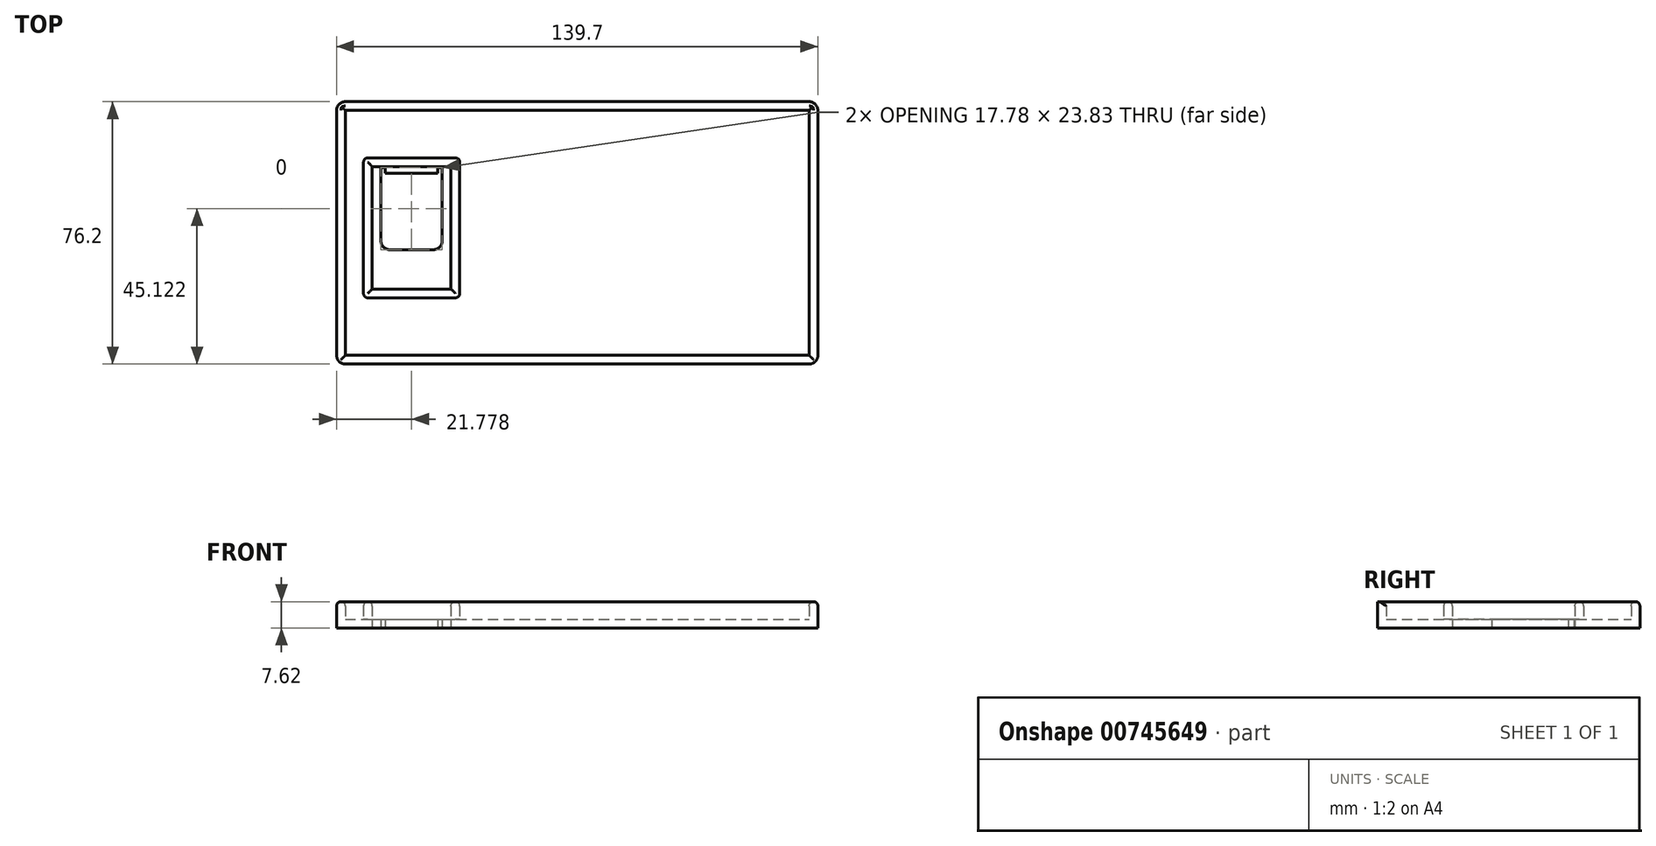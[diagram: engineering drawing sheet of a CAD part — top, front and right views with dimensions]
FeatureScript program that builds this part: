
annotation { "Feature Type Name" : "Feature", "Feature Type Description" : "" }
export const myFeature = defineFeature(function(context is Context, id is Id, definition is map)
    precondition{}
    {
        {
            var Q0;
            Q0=qCreatedBy(makeId("Top.planeOp"),FACE);
            var sketch = newSketch(context, id + "F0", { "sketchPlane" : qUnion([Q0])});
            skLineSegment(sketch, "E0.bottom", {"start": v(-71.99, 34.55) * mm, "end": v(67.71, 34.55) * mm});
            skLineSegment(sketch, "E0.top", {"start": v(-71.99, -41.65) * mm, "end": v(67.71, -41.65) * mm});
            skLineSegment(sketch, "E0.left", {"start": v(-71.99, 34.55) * mm, "end": v(-71.99, -41.65) * mm});
            skLineSegment(sketch, "E0.right", {"start": v(67.71, 34.55) * mm, "end": v(67.71, -41.65) * mm});
            skLineSegment(sketch, "E1.bottom", {"start": v(-69.45, -39.12) * mm, "end": v(65.17, -39.12) * mm});
            skLineSegment(sketch, "E1.top", {"start": v(-69.45, 32.01) * mm, "end": v(65.17, 32.01) * mm});
            skLineSegment(sketch, "E1.left", {"start": v(-69.45, -39.12) * mm, "end": v(-69.45, 32.01) * mm});
            skLineSegment(sketch, "E1.right", {"start": v(65.17, -39.12) * mm, "end": v(65.17, 32.01) * mm});
            skLineSegment(sketch, "E2", {"start": v(-69.45, 32.01) * mm, "end": v(-71.99, 34.55) * mm, "construction": true});
            skLineSegment(sketch, "E3", {"start": v(-71.99, -41.65) * mm, "end": v(-69.45, -39.12) * mm, "construction": true});
            skLineSegment(sketch, "E4", {"start": v(67.71, -41.65) * mm, "end": v(65.17, -39.12) * mm, "construction": true});
            skLineSegment(sketch, "E5", {"start": v(67.71, 34.55) * mm, "end": v(65.17, 32.01) * mm, "construction": true});
            skLineSegment(sketch, "E6", {"start": v(-71.99, 32.01) * mm, "end": v(-69.45, 32.01) * mm, "construction": true});
            skLineSegment(sketch, "E7", {"start": v(-69.45, 32.01) * mm, "end": v(-69.45, 34.55) * mm, "construction": true});
            skArc(sketch, "E8", {"start": v(-69.45, 34.55) * mm, "mid": v(-71.24, 33.8) * mm, "end": v(-71.99, 32.01) * mm});
            skLineSegment(sketch, "E9", {"start": v(-69.45, -39.12) * mm, "end": v(-69.45, -41.65) * mm, "construction": true});
            skLineSegment(sketch, "E10", {"start": v(-71.99, -39.12) * mm, "end": v(-69.45, -39.12) * mm, "construction": true});
            skLineSegment(sketch, "E11", {"start": v(65.17, 32.01) * mm, "end": v(67.71, 32.01) * mm, "construction": true});
            skLineSegment(sketch, "E12", {"start": v(65.17, 32.01) * mm, "end": v(65.17, 34.55) * mm, "construction": true});
            skArc(sketch, "E13", {"start": v(67.71, 32.01) * mm, "mid": v(66.96, 33.8) * mm, "end": v(65.17, 34.55) * mm});
            skArc(sketch, "E14", {"start": v(-71.99, -39.12) * mm, "mid": v(-71.24, -40.91) * mm, "end": v(-69.45, -41.65) * mm});
            skLineSegment(sketch, "E15", {"start": v(65.17, -39.12) * mm, "end": v(65.17, -41.65) * mm, "construction": true});
            skLineSegment(sketch, "E16", {"start": v(67.71, -39.14) * mm, "end": v(65.17, -39.12) * mm, "construction": true});
            skArc(sketch, "E17", {"start": v(65.17, -41.65) * mm, "mid": v(66.96, -40.92) * mm, "end": v(67.71, -39.14) * mm});
            skLineSegment(sketch, "E18.bottom", {"start": v(-62.91, 18.23) * mm, "end": v(-37.51, 18.23) * mm});
            skLineSegment(sketch, "E18.top", {"start": v(-62.91, -22.41) * mm, "end": v(-37.51, -22.41) * mm});
            skLineSegment(sketch, "E18.left", {"start": v(-64.18, 16.96) * mm, "end": v(-64.18, -21.14) * mm});
            skLineSegment(sketch, "E18.right", {"start": v(-36.24, 16.96) * mm, "end": v(-36.24, -21.14) * mm});
            skArc(sketch, "E19.filletArc", {"start": v(-62.91, 18.23) * mm, "mid": v(-63.8, 17.85) * mm, "end": v(-64.18, 16.96) * mm});
            skArc(sketch, "E20.filletArc", {"start": v(-36.24, 16.96) * mm, "mid": v(-36.61, 17.85) * mm, "end": v(-37.51, 18.23) * mm});
            skArc(sketch, "E21.filletArc", {"start": v(-37.51, -22.41) * mm, "mid": v(-36.61, -22.04) * mm, "end": v(-36.24, -21.14) * mm});
            skArc(sketch, "E22.filletArc", {"start": v(-64.18, -21.14) * mm, "mid": v(-63.8, -22.04) * mm, "end": v(-62.91, -22.41) * mm});
            skLineSegment(sketch, "E23.bottom", {"start": v(-61.64, -19.87) * mm, "end": v(-38.78, -19.87) * mm});
            skLineSegment(sketch, "E23.top", {"start": v(-61.64, 15.69) * mm, "end": v(-38.78, 15.69) * mm});
            skLineSegment(sketch, "E23.left", {"start": v(-61.64, -19.87) * mm, "end": v(-61.64, 15.69) * mm});
            skLineSegment(sketch, "E23.right", {"start": v(-38.78, -19.87) * mm, "end": v(-38.78, 15.69) * mm});
            skPoint(sketch, "E24.startSnap0", {"position": v(-36.24, -2.1) * mm});
            skPoint(sketch, "E24.endSnap0", {"position": v(-38.78, -2.1) * mm});
            skLineSegment(sketch, "E25", {"start": v(-64.18, -2.1) * mm, "end": v(-61.64, -2.1) * mm, "construction": true});
            skLineSegment(sketch, "E26", {"start": v(-50.21, -22.41) * mm, "end": v(-50.21, -19.87) * mm, "construction": true});
            skLineSegment(sketch, "E27", {"start": v(-36.24, -2.1) * mm, "end": v(-38.78, -2.1) * mm, "construction": true});
            skLineSegment(sketch, "E28", {"start": v(-50.21, 18.23) * mm, "end": v(-50.21, 15.69) * mm, "construction": true});
            skLineSegment(sketch, "E29.bottom", {"start": v(-59.1, 15.39) * mm, "end": v(-41.32, 15.39) * mm, "construction": true});
            skLineSegment(sketch, "E29.top", {"start": v(-56.56, -8.44) * mm, "end": v(-43.86, -8.44) * mm});
            skLineSegment(sketch, "E29.left", {"start": v(-59.1, 15.39) * mm, "end": v(-59.1, -5.9) * mm});
            skLineSegment(sketch, "E29.right", {"start": v(-41.32, 15.39) * mm, "end": v(-41.32, -5.9) * mm});
            skLineSegment(sketch, "E30", {"start": v(-61.64, -2.1) * mm, "end": v(-59.1, -2.1) * mm, "construction": true});
            skLineSegment(sketch, "E31", {"start": v(-38.78, -2.1) * mm, "end": v(-41.32, -2.1) * mm, "construction": true});
            skLineSegment(sketch, "E32", {"start": v(-50.21, -19.87) * mm, "end": v(-50.21, -8.44) * mm, "construction": true});
            skLineSegment(sketch, "E33", {"start": v(-50.21, 15.69) * mm, "end": v(-50.21, 13.15) * mm, "construction": true});
            skPoint(sketch, "E34.visualSharp", {"position": v(-59.1, -8.44) * mm});
            skArc(sketch, "E34.filletArc", {"start": v(-59.1, -5.9) * mm, "mid": v(-58.36, -7.7) * mm, "end": v(-56.56, -8.44) * mm});
            skPoint(sketch, "E35.visualSharp", {"position": v(-41.32, -8.44) * mm});
            skArc(sketch, "E35.filletArc", {"start": v(-43.86, -8.44) * mm, "mid": v(-42.07, -7.7) * mm, "end": v(-41.32, -5.9) * mm});
            skLineSegment(sketch, "E36", {"start": v(-57.83, 13.78) * mm, "end": v(-57.83, 15.39) * mm});
            skLineSegment(sketch, "E37", {"start": v(-56.56, 15.39) * mm, "end": v(-56.56, 13.78) * mm});
            skLineSegment(sketch, "E38", {"start": v(-55.3, 15.39) * mm, "end": v(-55.3, 13.78) * mm});
            skLineSegment(sketch, "E39", {"start": v(-52.75, 15.39) * mm, "end": v(-52.75, 13.78) * mm});
            skLineSegment(sketch, "E40", {"start": v(-54.02, 15.39) * mm, "end": v(-54.02, 13.78) * mm});
            skLineSegment(sketch, "E41", {"start": v(-51.48, 15.39) * mm, "end": v(-51.48, 13.78) * mm});
            skLineSegment(sketch, "E42", {"start": v(-48.94, 15.39) * mm, "end": v(-48.94, 13.78) * mm});
            skLineSegment(sketch, "E43", {"start": v(-46.4, 15.39) * mm, "end": v(-46.4, 13.78) * mm});
            skLineSegment(sketch, "E44", {"start": v(-47.67, 15.39) * mm, "end": v(-47.67, 13.78) * mm});
            skLineSegment(sketch, "E45", {"start": v(-45.13, 15.39) * mm, "end": v(-45.13, 13.78) * mm});
            skLineSegment(sketch, "E46", {"start": v(-42.6, 15.39) * mm, "end": v(-42.6, 13.78) * mm});
            skLineSegment(sketch, "E47", {"start": v(-43.86, 15.39) * mm, "end": v(-43.86, 13.78) * mm});
            skLineSegment(sketch, "E48", {"start": v(-50.21, 13.15) * mm, "end": v(-50.21, 13.78) * mm});
            skLineSegment(sketch, "E49", {"start": v(-50.21, -5.27) * mm, "end": v(-50.21, -2.1) * mm});
            skLineSegment(sketch, "E50", {"start": v(-50.21, -2.1) * mm, "end": v(-50.21, 1.08) * mm});
            skLineSegment(sketch, "E51", {"start": v(-50.21, 1.08) * mm, "end": v(-50.21, 4.26) * mm});
            skLineSegment(sketch, "E52", {"start": v(-50.21, 4.26) * mm, "end": v(-50.21, 7.43) * mm});
            skLineSegment(sketch, "E53", {"start": v(-50.21, 7.43) * mm, "end": v(-50.21, 10.6) * mm});
            skLineSegment(sketch, "E54", {"start": v(-59.1, 15.39) * mm, "end": v(-57.83, 15.39) * mm});
            skPoint(sketch, "E55.endSnap0", {"position": v(-59.1, 4.74) * mm});
            skLineSegment(sketch, "E56", {"start": v(-42.6, 15.39) * mm, "end": v(-41.32, 15.39) * mm});
            skLineSegment(sketch, "E57", {"start": v(-50.21, 10.6) * mm, "end": v(-50.21, 13.78) * mm});
            skPoint(sketch, "E58.endSnap0", {"position": v(-50.21, 12.2) * mm});
            skLineSegment(sketch, "E59", {"start": v(-59.1, 13.78) * mm, "end": v(-58.47, 13.78) * mm});
            skLineSegment(sketch, "E60", {"start": v(-58.47, 13.78) * mm, "end": v(-57.83, 13.78) * mm});
            skLineSegment(sketch, "E61", {"start": v(-57.83, 13.78) * mm, "end": v(-57.2, 13.78) * mm});
            skLineSegment(sketch, "E62", {"start": v(-57.2, 13.78) * mm, "end": v(-56.56, 13.78) * mm});
            skLineSegment(sketch, "E63", {"start": v(-56.56, 13.78) * mm, "end": v(-55.93, 13.78) * mm});
            skLineSegment(sketch, "E64", {"start": v(-55.93, 13.78) * mm, "end": v(-55.3, 13.78) * mm});
            skLineSegment(sketch, "E65", {"start": v(-55.3, 13.78) * mm, "end": v(-54.66, 13.78) * mm});
            skLineSegment(sketch, "E66", {"start": v(-54.66, 13.78) * mm, "end": v(-54.02, 13.78) * mm});
            skLineSegment(sketch, "E67", {"start": v(-54.02, 13.78) * mm, "end": v(-53.39, 13.78) * mm});
            skLineSegment(sketch, "E68", {"start": v(-53.39, 13.78) * mm, "end": v(-52.75, 13.78) * mm});
            skLineSegment(sketch, "E69", {"start": v(-52.75, 13.78) * mm, "end": v(-52.12, 13.78) * mm});
            skLineSegment(sketch, "E70", {"start": v(-52.12, 13.78) * mm, "end": v(-51.48, 13.78) * mm});
            skLineSegment(sketch, "E71", {"start": v(-51.48, 13.78) * mm, "end": v(-50.85, 13.78) * mm});
            skLineSegment(sketch, "E72", {"start": v(-50.85, 13.78) * mm, "end": v(-50.21, 13.78) * mm});
            skLineSegment(sketch, "E73", {"start": v(-50.21, 13.78) * mm, "end": v(-49.58, 13.78) * mm});
            skLineSegment(sketch, "E74", {"start": v(-49.58, 13.78) * mm, "end": v(-48.94, 13.78) * mm});
            skLineSegment(sketch, "E75", {"start": v(-48.94, 13.78) * mm, "end": v(-48.3, 13.78) * mm});
            skLineSegment(sketch, "E76", {"start": v(-48.3, 13.78) * mm, "end": v(-47.67, 13.78) * mm});
            skLineSegment(sketch, "E77", {"start": v(-47.67, 13.78) * mm, "end": v(-47.04, 13.78) * mm});
            skLineSegment(sketch, "E78", {"start": v(-47.04, 13.78) * mm, "end": v(-46.4, 13.78) * mm});
            skLineSegment(sketch, "E79", {"start": v(-46.4, 13.78) * mm, "end": v(-45.77, 13.78) * mm});
            skLineSegment(sketch, "E80", {"start": v(-45.77, 13.78) * mm, "end": v(-45.13, 13.78) * mm});
            skLineSegment(sketch, "E81", {"start": v(-45.13, 13.78) * mm, "end": v(-44.5, 13.78) * mm});
            skLineSegment(sketch, "E82", {"start": v(-44.5, 13.78) * mm, "end": v(-43.86, 13.78) * mm});
            skLineSegment(sketch, "E83", {"start": v(-43.86, 13.78) * mm, "end": v(-43.23, 13.78) * mm});
            skLineSegment(sketch, "E84", {"start": v(-43.23, 13.78) * mm, "end": v(-42.6, 13.78) * mm});
            skLineSegment(sketch, "E85", {"start": v(-42.6, 13.78) * mm, "end": v(-41.96, 13.78) * mm});
            skLineSegment(sketch, "E86", {"start": v(-41.96, 13.78) * mm, "end": v(-41.32, 13.78) * mm});
            skLineSegment(sketch, "E87", {"start": v(-50.21, 10.6) * mm, "end": v(-50.8, 10.6) * mm, "construction": true});
            skLineSegment(sketch, "E88", {"start": v(-50.8, 10.6) * mm, "end": v(-51.38, 10.6) * mm, "construction": true});
            skLineSegment(sketch, "E89", {"start": v(-51.38, 10.6) * mm, "end": v(-51.96, 10.6) * mm, "construction": true});
            skLineSegment(sketch, "E90", {"start": v(-51.96, 10.6) * mm, "end": v(-52.55, 10.6) * mm, "construction": true});
            skLineSegment(sketch, "E91", {"start": v(-52.55, 10.6) * mm, "end": v(-53.13, 10.6) * mm, "construction": true});
            skLineSegment(sketch, "E92", {"start": v(-53.13, 10.6) * mm, "end": v(-53.72, 10.6) * mm, "construction": true});
            skLineSegment(sketch, "E93", {"start": v(-53.72, 10.6) * mm, "end": v(-54.3, 10.6) * mm, "construction": true});
            skLineSegment(sketch, "E94", {"start": v(-54.3, 10.6) * mm, "end": v(-54.89, 10.6) * mm, "construction": true});
            skLineSegment(sketch, "E95", {"start": v(-54.89, 10.6) * mm, "end": v(-55.47, 10.6) * mm, "construction": true});
            skLineSegment(sketch, "E96", {"start": v(-55.47, 10.6) * mm, "end": v(-56.05, 10.6) * mm, "construction": true});
            skLineSegment(sketch, "E97", {"start": v(-56.05, 10.6) * mm, "end": v(-56.64, 10.6) * mm, "construction": true});
            skLineSegment(sketch, "E98", {"start": v(-56.64, 10.6) * mm, "end": v(-57.22, 10.6) * mm, "construction": true});
            skLineSegment(sketch, "E99", {"start": v(-57.22, 10.6) * mm, "end": v(-57.8, 10.6) * mm, "construction": true});
            skLineSegment(sketch, "E100", {"start": v(-50.21, 4.26) * mm, "end": v(-50.75, 4.26) * mm, "construction": true});
            skLineSegment(sketch, "E101", {"start": v(-50.75, 4.26) * mm, "end": v(-51.28, 4.26) * mm, "construction": true});
            skLineSegment(sketch, "E102", {"start": v(-51.28, 4.26) * mm, "end": v(-51.81, 4.26) * mm, "construction": true});
            skLineSegment(sketch, "E103", {"start": v(-51.81, 4.26) * mm, "end": v(-52.35, 4.26) * mm, "construction": true});
            skLineSegment(sketch, "E104", {"start": v(-52.35, 4.26) * mm, "end": v(-52.88, 4.26) * mm, "construction": true});
            skLineSegment(sketch, "E105", {"start": v(-52.88, 4.26) * mm, "end": v(-53.41, 4.26) * mm, "construction": true});
            skLineSegment(sketch, "E106", {"start": v(-53.41, 4.26) * mm, "end": v(-53.95, 4.26) * mm, "construction": true});
            skLineSegment(sketch, "E107", {"start": v(-53.95, 4.26) * mm, "end": v(-54.48, 4.26) * mm, "construction": true});
            skLineSegment(sketch, "E108", {"start": v(-54.48, 4.26) * mm, "end": v(-55.01, 4.26) * mm, "construction": true});
            skLineSegment(sketch, "E109", {"start": v(-50.21, 1.08) * mm, "end": v(-50.72, 1.08) * mm, "construction": true});
            skLineSegment(sketch, "E110", {"start": v(-50.72, 1.08) * mm, "end": v(-51.23, 1.08) * mm, "construction": true});
            skLineSegment(sketch, "E111", {"start": v(-51.23, 1.08) * mm, "end": v(-51.74, 1.08) * mm, "construction": true});
            skLineSegment(sketch, "E112", {"start": v(-51.74, 1.08) * mm, "end": v(-52.24, 1.08) * mm, "construction": true});
            skLineSegment(sketch, "E113", {"start": v(-52.24, 1.08) * mm, "end": v(-52.75, 1.08) * mm, "construction": true});
            skLineSegment(sketch, "E114", {"start": v(-52.75, 1.08) * mm, "end": v(-53.26, 1.08) * mm, "construction": true});
            skLineSegment(sketch, "E115", {"start": v(-53.26, 1.08) * mm, "end": v(-53.77, 1.08) * mm, "construction": true});
            skLineSegment(sketch, "E116", {"start": v(-50.21, 7.43) * mm, "end": v(-50.77, 7.43) * mm, "construction": true});
            skLineSegment(sketch, "E117", {"start": v(-50.77, 7.43) * mm, "end": v(-51.33, 7.43) * mm, "construction": true});
            skLineSegment(sketch, "E118", {"start": v(-51.33, 7.43) * mm, "end": v(-51.89, 7.43) * mm, "construction": true});
            skLineSegment(sketch, "E119", {"start": v(-51.89, 7.43) * mm, "end": v(-52.45, 7.43) * mm, "construction": true});
            skLineSegment(sketch, "E120", {"start": v(-52.45, 7.43) * mm, "end": v(-53, 7.43) * mm, "construction": true});
            skLineSegment(sketch, "E121", {"start": v(-53, 7.43) * mm, "end": v(-53.56, 7.43) * mm, "construction": true});
            skLineSegment(sketch, "E122", {"start": v(-53.56, 7.43) * mm, "end": v(-54.12, 7.43) * mm, "construction": true});
            skLineSegment(sketch, "E123", {"start": v(-54.12, 7.43) * mm, "end": v(-54.68, 7.43) * mm, "construction": true});
            skLineSegment(sketch, "E124", {"start": v(-54.68, 7.43) * mm, "end": v(-55.24, 7.43) * mm, "construction": true});
            skLineSegment(sketch, "E125", {"start": v(-55.24, 7.43) * mm, "end": v(-55.8, 7.43) * mm, "construction": true});
            skLineSegment(sketch, "E126", {"start": v(-55.8, 7.43) * mm, "end": v(-56.36, 7.43) * mm, "construction": true});
            skLineSegment(sketch, "E127", {"start": v(-50.21, 13.15) * mm, "end": v(-50.82, 13.15) * mm, "construction": true});
            skLineSegment(sketch, "E128", {"start": v(-50.82, 13.15) * mm, "end": v(-51.43, 13.15) * mm, "construction": true});
            skLineSegment(sketch, "E129", {"start": v(-51.43, 13.15) * mm, "end": v(-52.04, 13.15) * mm, "construction": true});
            skLineSegment(sketch, "E130", {"start": v(-52.04, 13.15) * mm, "end": v(-52.65, 13.15) * mm, "construction": true});
            skLineSegment(sketch, "E131", {"start": v(-52.65, 13.15) * mm, "end": v(-53.26, 13.15) * mm, "construction": true});
            skLineSegment(sketch, "E132", {"start": v(-53.26, 13.15) * mm, "end": v(-53.87, 13.15) * mm, "construction": true});
            skLineSegment(sketch, "E133", {"start": v(-53.87, 13.15) * mm, "end": v(-54.48, 13.15) * mm, "construction": true});
            skLineSegment(sketch, "E134", {"start": v(-54.48, 13.15) * mm, "end": v(-55.09, 13.15) * mm, "construction": true});
            skLineSegment(sketch, "E135", {"start": v(-55.09, 13.15) * mm, "end": v(-55.7, 13.15) * mm, "construction": true});
            skLineSegment(sketch, "E136", {"start": v(-55.7, 13.15) * mm, "end": v(-56.3, 13.15) * mm, "construction": true});
            skLineSegment(sketch, "E137", {"start": v(-56.3, 13.15) * mm, "end": v(-56.92, 13.15) * mm, "construction": true});
            skLineSegment(sketch, "E138", {"start": v(-56.92, 13.15) * mm, "end": v(-57.53, 13.15) * mm, "construction": true});
            skLineSegment(sketch, "E139", {"start": v(-57.53, 13.15) * mm, "end": v(-58.14, 13.15) * mm, "construction": true});
            skLineSegment(sketch, "E140", {"start": v(-50.21, -2.1) * mm, "end": v(-50.7, -2.1) * mm, "construction": true});
            skLineSegment(sketch, "E141", {"start": v(-50.7, -2.1) * mm, "end": v(-51.18, -2.1) * mm, "construction": true});
            skLineSegment(sketch, "E142", {"start": v(-51.18, -2.1) * mm, "end": v(-51.66, -2.1) * mm, "construction": true});
            skLineSegment(sketch, "E143", {"start": v(-51.66, -2.1) * mm, "end": v(-52.14, -2.1) * mm, "construction": true});
            skLineSegment(sketch, "E144", {"start": v(-52.14, -2.1) * mm, "end": v(-52.62, -2.1) * mm, "construction": true});
            skLineSegment(sketch, "E145", {"start": v(-50.21, -5.27) * mm, "end": v(-50.67, -5.27) * mm, "construction": true});
            skLineSegment(sketch, "E146", {"start": v(-50.67, -5.27) * mm, "end": v(-51.13, -5.27) * mm, "construction": true});
            skLineSegment(sketch, "E147", {"start": v(-51.13, -5.27) * mm, "end": v(-51.58, -5.27) * mm, "construction": true});
            skLineSegment(sketch, "E148", {"start": v(-58.14, 13.15) * mm, "end": v(-58.75, 13.15) * mm, "construction": true});
            skFitSpline(sketch, "E149", {"points": [v(-50.21, -8.44) * mm, v(-51.13, -5.27) * mm, v(-52.14, -2.1) * mm, v(-53.26, 1.08) * mm, v(-55.01, 4.26) * mm, v(-56.36, 7.43) * mm, v(-57.8, 10.6) * mm, v(-58.47, 13.78) * mm], "startDerivative": vector(-6.27, 22.58) * mm, "endDerivative": vector(-3.23, 23) * mm});
            skFitSpline(sketch, "E150", {"points": [v(-50.21, -6.86) * mm, v(-50.67, -5.27) * mm, v(-51.66, -2.1) * mm, v(-52.75, 1.08) * mm, v(-54.48, 4.26) * mm, v(-55.8, 7.43) * mm, v(-57.22, 10.6) * mm, v(-57.83, 13.78) * mm], "startDerivative": vector(-3.84, 13.87) * mm, "endDerivative": vector(-2.7, 22.05) * mm});
            skFitSpline(sketch, "E151", {"points": [v(-50.21, -5.27) * mm, v(-51.18, -2.1) * mm, v(-52.24, 1.08) * mm, v(-53.95, 4.26) * mm, v(-55.24, 7.43) * mm, v(-56.64, 10.6) * mm, v(-57.2, 13.78) * mm], "startDerivative": vector(-6, 19.24) * mm, "endDerivative": vector(-2.07, 19.76) * mm});
            skFitSpline(sketch, "E152", {"points": [v(-50.21, -3.68) * mm, v(-50.7, -2.1) * mm, v(-51.74, 1.08) * mm, v(-53.41, 4.26) * mm, v(-54.68, 7.43) * mm, v(-56.05, 10.6) * mm, v(-56.56, 13.78) * mm], "startDerivative": vector(-4.03, 11.66) * mm, "endDerivative": vector(-1.48, 18.76) * mm});
            skFitSpline(sketch, "E153", {"points": [v(-50.21, -2.1) * mm, v(-51.23, 1.08) * mm, v(-52.88, 4.26) * mm, v(-54.12, 7.43) * mm, v(-55.47, 10.6) * mm, v(-55.93, 13.78) * mm], "startDerivative": vector(-4.2, 16.2) * mm, "endDerivative": vector(-1.13, 16.5) * mm});
            skFitSpline(sketch, "E154", {"points": [v(-50.21, -0.5) * mm, v(-50.72, 1.08) * mm, v(-52.35, 4.26) * mm, v(-53.56, 7.43) * mm, v(-54.89, 10.6) * mm, v(-55.3, 13.78) * mm], "startDerivative": vector(-2.39, 9.82) * mm, "endDerivative": vector(-0.77, 15.51) * mm});
            skFitSpline(sketch, "E155", {"points": [v(-50.21, 1.08) * mm, v(-51.81, 4.26) * mm, v(-53, 7.43) * mm, v(-54.3, 10.6) * mm, v(-54.66, 13.78) * mm], "startDerivative": vector(-6.75, 12.31) * mm, "endDerivative": vector(-0.44, 13.22) * mm});
            skFitSpline(sketch, "E156", {"points": [v(-50.21, 2.67) * mm, v(-51.28, 4.26) * mm, v(-52.45, 7.43) * mm, v(-53.72, 10.6) * mm, v(-54.02, 13.78) * mm], "startDerivative": vector(-5.58, 6.94) * mm, "endDerivative": vector(-0.2, 12.39) * mm});
            skLineSegment(sketch, "E157", {"start": v(-50.21, -5.27) * mm, "end": v(-50.21, -8.44) * mm});
            skSolve(sketch);
        }
        {
            var Q0;
            Q0=makeQuery(id+"F0.imprint","IMPRINT",FACE,{"disambiguationData":[TD([[makeQuery(id+"F0.imprint","IMPRINT",EDGE,{"derivedFrom":sQuery(id+"F0.wireOp",EDGE,"E1.top")}),1.0]])]});
            var Q1;
            {var subQ0=sQuery(id+"F0.wireOp",EDGE,"E19.filletArc");Q1=makeQuery(id+"F0.imprint","IMPRINT",FACE,{"disambiguationData":[TD([[makeQuery(id+"F0.imprint","IMPRINT",EDGE,{"derivedFrom":subQ0}),1.0]])]});}
            var Q2;
            {var subQ4=sQuery(id+"F0.wireOp",EDGE,"E20.filletArc");Q2=makeQuery(id+"F0.imprint","IMPRINT",FACE,{"disambiguationData":[TD([[makeQuery(id+"F0.imprint","IMPRINT",EDGE,{"derivedFrom":subQ4}),1.0]])]});}
            var Q3;
            {var subQ0=sQuery(id+"F0.wireOp",EDGE,"E22.filletArc");Q3=makeQuery(id+"F0.imprint","IMPRINT",FACE,{"disambiguationData":[TD([[makeQuery(id+"F0.imprint","IMPRINT",EDGE,{"derivedFrom":subQ0}),1.0]])]});}
            var Q4;
            {var subQ0=sQuery(id+"F0.wireOp",EDGE,"E21.filletArc");Q4=makeQuery(id+"F0.imprint","IMPRINT",FACE,{"disambiguationData":[TD([[makeQuery(id+"F0.imprint","IMPRINT",EDGE,{"derivedFrom":subQ0}),1.0]])]});}
            extrude(context, id + "F1", {"entities" : qUnion([Q0, Q1, Q2, Q3, Q4]), "depth" : 7.62 * mm, "offsetDistance" : 25.4 * mm});
        }
        {
            var Q0;
            Q0=makeQuery(id+"F0.imprint","IMPRINT",FACE,{"disambiguationData":[TD([[makeQuery(id+"F0.imprint","IMPRINT",EDGE,{"derivedFrom":sQuery(id+"F0.wireOp",EDGE,"E1.bottom")}),1.0]])]});
            var Q1;
            {var subQ4=sQuery(id+"F0.wireOp",EDGE,"E23.left");var subQ6=sQuery(id+"F0.wireOp",EDGE,"E23.bottom");var subQ9=makeQuery(id+"F0.imprint","INTERSECT",VERTEX,{"derivedFrom":[subQ6,subQ4]});Q1=makeQuery(id+"F0.imprint","IMPRINT",FACE,{"disambiguationData":[TD([[makeQuery(id+"F0.imprint","IMPRINT",EDGE,{"disambiguationData":[TD([[subQ9,-1.0]])],"derivedFrom":subQ6}),1.0]])]});}
            extrude(context, id + "F2", {"entities" : qUnion([Q0, Q1]), "operationType" : NewBodyOperationType.ADD, "depth" : 2.54 * mm, "offsetDistance" : 25.4 * mm});
        }
        {
            var Q0;
            Q0=makeQuery(id+"F1.opExtrude","CAP_EDGE",EDGE,{"disambiguationData":[OSD([sQuery(id+"F0.wireOp",EDGE,"E8")])],"isStart":false});
            fillet(context, id + "F3", {"entities" : qUnion([Q0]), "radius" : 1.27 * mm, "tangentPropagation" : true, "allowEdgeOverflow" : false});
        }
        {
            var Q0;
            Q0=makeQuery(id+"F1.opExtrude","CAP_EDGE",EDGE,{"disambiguationData":[OSD([sQuery(id+"F0.wireOp",EDGE,"E1.top")])],"isStart":false});
            var Q1;
            Q1=makeQuery(id+"F1.opExtrude","CAP_EDGE",EDGE,{"disambiguationData":[OSD([sQuery(id+"F0.wireOp",EDGE,"E1.left")])],"isStart":false});
            var Q2;
            Q2=makeQuery(id+"F1.opExtrude","CAP_EDGE",EDGE,{"disambiguationData":[OSD([sQuery(id+"F0.wireOp",EDGE,"E1.right")])],"isStart":false});
            fillet(context, id + "F4", {"entities" : qUnion([Q0, Q1, Q2]), "radius" : 1.27 * mm, "tangentPropagation" : true, "allowEdgeOverflow" : false});
        }
        {
            var Q0;
            Q0=makeQuery(id+"F1.opExtrude","CAP_EDGE",EDGE,{"disambiguationData":[OSD([sQuery(id+"F0.wireOp",EDGE,"E1.bottom")])],"isStart":false});
            fillet(context, id + "F5", {"entities" : qUnion([Q0]), "radius" : 1.27 * mm, "tangentPropagation" : true, "allowEdgeOverflow" : false});
        }
        {
            var Q0;
            Q0=makeQuery(id+"F1.opExtrude","CAP_EDGE",EDGE,{"disambiguationData":[OSD([sQuery(id+"F0.wireOp",EDGE,"E23.left")])],"isStart":false});
            var Q1;
            Q1=makeQuery(id+"F1.opExtrude","CAP_EDGE",EDGE,{"disambiguationData":[OSD([sQuery(id+"F0.wireOp",EDGE,"E18.left")])],"isStart":false});
            var Q2;
            Q2=makeQuery(id+"F1.opExtrude","CAP_EDGE",EDGE,{"disambiguationData":[OSD([sQuery(id+"F0.wireOp",EDGE,"E18.top")])],"isStart":false});
            var Q3;
            Q3=makeQuery(id+"F1.opExtrude","CAP_EDGE",EDGE,{"disambiguationData":[OSD([sQuery(id+"F0.wireOp",EDGE,"E22.filletArc")])],"isStart":false});
            var Q4;
            Q4=makeQuery(id+"F1.opExtrude","CAP_EDGE",EDGE,{"disambiguationData":[OSD([sQuery(id+"F0.wireOp",EDGE,"E21.filletArc")])],"isStart":false});
            var Q5;
            Q5=makeQuery(id+"F1.opExtrude","CAP_EDGE",EDGE,{"disambiguationData":[OSD([sQuery(id+"F0.wireOp",EDGE,"E18.right")])],"isStart":false});
            var Q6;
            Q6=makeQuery(id+"F1.opExtrude","CAP_EDGE",EDGE,{"disambiguationData":[OSD([sQuery(id+"F0.wireOp",EDGE,"E23.right")])],"isStart":false});
            var Q7;
            Q7=makeQuery(id+"F1.opExtrude","CAP_EDGE",EDGE,{"disambiguationData":[OSD([sQuery(id+"F0.wireOp",EDGE,"E18.bottom")])],"isStart":false});
            var Q8;
            Q8=makeQuery(id+"F1.opExtrude","CAP_EDGE",EDGE,{"disambiguationData":[OSD([sQuery(id+"F0.wireOp",EDGE,"E20.filletArc")])],"isStart":false});
            var Q9;
            Q9=makeQuery(id+"F1.opExtrude","CAP_EDGE",EDGE,{"disambiguationData":[OSD([sQuery(id+"F0.wireOp",EDGE,"E19.filletArc")])],"isStart":false});
            var Q10;
            Q10=makeQuery(id+"F1.opExtrude","CAP_EDGE",EDGE,{"disambiguationData":[OSD([sQuery(id+"F0.wireOp",EDGE,"E23.top")])],"isStart":false});
            fillet(context, id + "F6", {"entities" : qUnion([Q0, Q1, Q2, Q3, Q4, Q5, Q6, Q7, Q8, Q9, Q10]), "radius" : 1.27 * mm, "tangentPropagation" : true, "allowEdgeOverflow" : false});
        }
        {
            var Q0;
            Q0=makeQuery(id+"F1.opExtrude","CAP_EDGE",EDGE,{"disambiguationData":[OSD([sQuery(id+"F0.wireOp",EDGE,"E23.bottom")])],"isStart":false});
            fillet(context, id + "F7", {"entities" : qUnion([Q0]), "radius" : 1.27 * mm, "tangentPropagation" : true, "allowEdgeOverflow" : false});
        }
        {
            var Q0;
            {var subQ1=sQuery(id+"F0.wireOp",EDGE,"E36");Q0=makeQuery(id+"F0.imprint","IMPRINT",FACE,{"disambiguationData":[TD([[makeQuery(id+"F0.imprint","IMPRINT",EDGE,{"derivedFrom":subQ1}),-1.0]])]});}
            extrude(context, id + "F8", {"entities" : qUnion([Q0]), "operationType" : NewBodyOperationType.ADD, "depth" : 2.54 * mm, "offsetDistance" : 25.4 * mm});
        }
        {
            var Q0;
            {var subQ0=sQuery(id+"F0.wireOp",EDGE,"saNld0ps-bPU7-SiEP-Jv2h-3yJP6bNYpzAE");Q0=makeQuery(id+"F0.imprint","IMPRINT",FACE,{"disambiguationData":[TD([[makeQuery(id+"F0.imprint","IMPRINT",EDGE,{"derivedFrom":subQ0}),1.0]])]});}
            var Q1;
            {var subQ0=sQuery(id+"F0.wireOp",EDGE,"saNld0ps-bPU7-SiEP-Jv2h-3yJP6bNYpzAE");Q1=makeQuery(id+"F0.imprint","IMPRINT",FACE,{"disambiguationData":[TD([[makeQuery(id+"F0.imprint","IMPRINT",EDGE,{"derivedFrom":subQ0}),-1.0]])]});}
            var Q2;
            {var subQ1=sQuery(id+"F0.wireOp",EDGE,"E46");Q2=makeQuery(id+"F0.imprint","IMPRINT",FACE,{"disambiguationData":[TD([[makeQuery(id+"F0.imprint","IMPRINT",EDGE,{"derivedFrom":subQ1}),-1.0]])]});}
            var Q3;
            {var subQ2=sQuery(id+"F0.wireOp",EDGE,"E38");Q3=makeQuery(id+"F0.imprint","IMPRINT",FACE,{"disambiguationData":[TD([[makeQuery(id+"F0.imprint","IMPRINT",EDGE,{"derivedFrom":subQ2}),1.0]])]});}
            var Q4;
            {var subQ1=sQuery(id+"F0.wireOp",EDGE,"E43");Q4=makeQuery(id+"F0.imprint","IMPRINT",FACE,{"disambiguationData":[TD([[makeQuery(id+"F0.imprint","IMPRINT",EDGE,{"derivedFrom":subQ1}),1.0]])]});}
            var Q5;
            {var subQ1=sQuery(id+"F0.wireOp",EDGE,"E39");Q5=makeQuery(id+"F0.imprint","IMPRINT",FACE,{"disambiguationData":[TD([[makeQuery(id+"F0.imprint","IMPRINT",EDGE,{"derivedFrom":subQ1}),1.0]])]});}
            var Q6;
            {var subQ0=sQuery(id+"F0.wireOp",EDGE,"E42");Q6=makeQuery(id+"F0.imprint","IMPRINT",FACE,{"disambiguationData":[TD([[makeQuery(id+"F0.imprint","IMPRINT",EDGE,{"derivedFrom":subQ0}),1.0]])]});}
            extrude(context, id + "F9", {"entities" : qUnion([Q0, Q1, Q2, Q3, Q4, Q5, Q6]), "depth" : 2.54 * mm, "offsetDistance" : 25.4 * mm});
        }
    });
